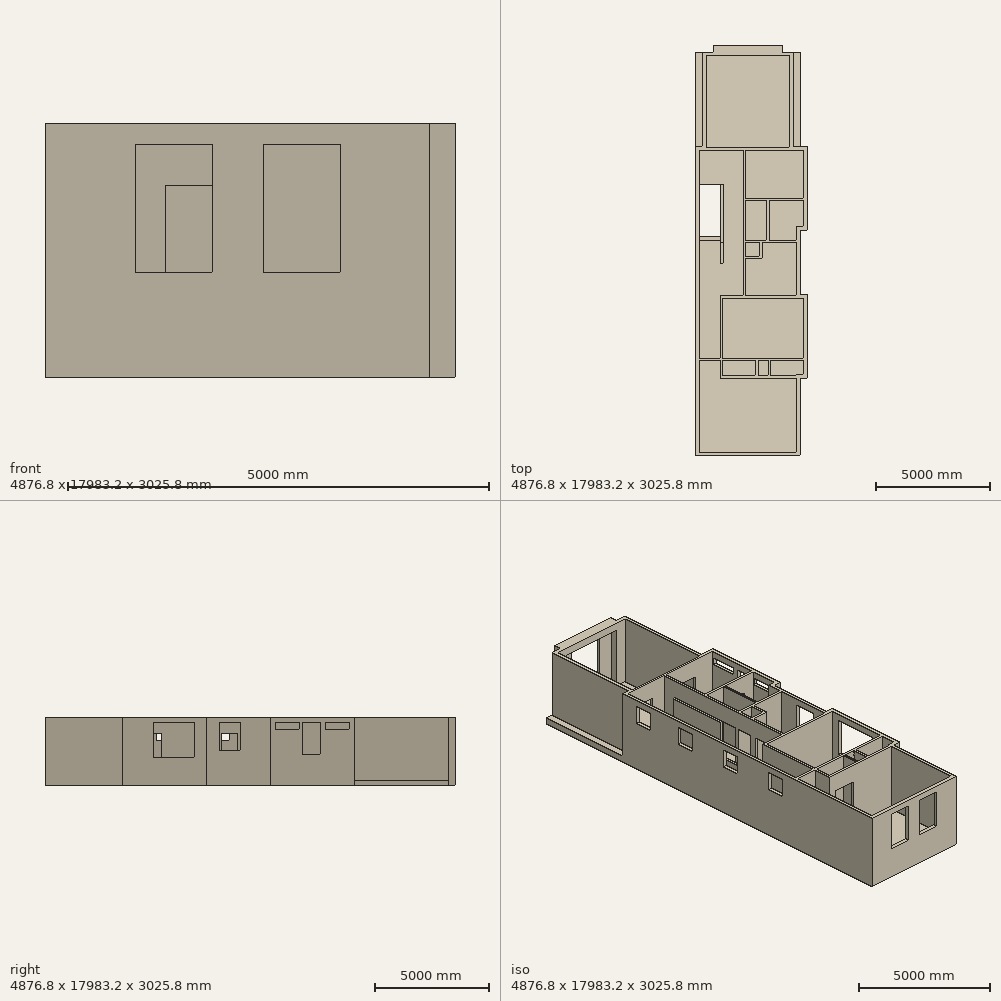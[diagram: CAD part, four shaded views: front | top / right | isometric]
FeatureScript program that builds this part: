
annotation { "Feature Type Name" : "Feature", "Feature Type Description" : "" }
export const myFeature = defineFeature(function(context is Context, id is Id, definition is map)
    precondition{}
    {
        {
            var Q0;
            Q0=qCreatedBy(makeId("Top.planeOp"),FACE);
            var sketch = newSketch(context, id + "F0", { "sketchPlane" : qUnion([Q0])});
            skLineSegment(sketch, "E0", {"start": v(4572, 0) * mm, "end": v(0, 0) * mm});
            skLineSegment(sketch, "E1", {"start": v(0, 0) * mm, "end": v(0, 17678.4) * mm});
            skLineSegment(sketch, "E2", {"start": v(0, 17678.4) * mm, "end": v(762, 17678.4) * mm});
            skLineSegment(sketch, "E3", {"start": v(762, 17678.4) * mm, "end": v(762, 17983.2) * mm});
            skLineSegment(sketch, "E4", {"start": v(762, 17983.2) * mm, "end": v(3810, 17983.2) * mm});
            skLineSegment(sketch, "E5", {"start": v(3810, 17983.2) * mm, "end": v(3810, 17678.4) * mm});
            skLineSegment(sketch, "E6", {"start": v(3810, 17678.4) * mm, "end": v(4572, 17678.4) * mm});
            skLineSegment(sketch, "E7", {"start": v(4572, 17678.4) * mm, "end": v(4572, 13538.2) * mm});
            skLineSegment(sketch, "E8", {"start": v(4572, 13538.2) * mm, "end": v(4876.8, 13538.2) * mm});
            skLineSegment(sketch, "E9", {"start": v(4876.8, 13538.2) * mm, "end": v(4876.8, 9880.6) * mm});
            skLineSegment(sketch, "E10", {"start": v(4876.8, 9880.6) * mm, "end": v(4572, 9880.6) * mm});
            skLineSegment(sketch, "E11", {"start": v(4572, 9880.6) * mm, "end": v(4572, 7048.5) * mm});
            skLineSegment(sketch, "E12", {"start": v(4572, 7048.5) * mm, "end": v(4876.8, 7048.5) * mm});
            skLineSegment(sketch, "E13", {"start": v(4876.8, 7048.5) * mm, "end": v(4876.8, 3390.9) * mm});
            skLineSegment(sketch, "E14", {"start": v(4876.8, 3390.9) * mm, "end": v(4572, 3390.9) * mm});
            skLineSegment(sketch, "E15", {"start": v(4572, 3390.9) * mm, "end": v(4572, 0) * mm});
            skSolve(sketch);
        }
        {
            var Q0;
            Q0=makeQuery(id+"F0.imprint","IMPRINT",FACE,{"disambiguationData":[TD([[makeQuery(id+"F0.imprint","IMPRINT",EDGE,{"derivedFrom":sQuery(id+"F0.wireOp",EDGE,"E0")}),-1.0]])]});
            extrude(context, id + "F1", {"entities" : qUnion([Q0]), "oppositeDirection" : true, "depth" : 254 * mm});
        }
        {
            var Q0;
            Q0=makeQuery(id+"F1.opExtrude","CAP_FACE",FACE,{"disambiguationData":[OSD([sQuery(id+"F0.wireOp",EDGE,"E0"),sQuery(id+"F0.wireOp",EDGE,"E1"),sQuery(id+"F0.wireOp",EDGE,"E2"),sQuery(id+"F0.wireOp",EDGE,"E3"),sQuery(id+"F0.wireOp",EDGE,"E4"),sQuery(id+"F0.wireOp",EDGE,"E5"),sQuery(id+"F0.wireOp",EDGE,"E6"),sQuery(id+"F0.wireOp",EDGE,"E7"),sQuery(id+"F0.wireOp",EDGE,"E8"),sQuery(id+"F0.wireOp",EDGE,"E9"),sQuery(id+"F0.wireOp",EDGE,"E10"),sQuery(id+"F0.wireOp",EDGE,"E11"),sQuery(id+"F0.wireOp",EDGE,"E12"),sQuery(id+"F0.wireOp",EDGE,"E13"),sQuery(id+"F0.wireOp",EDGE,"E14"),sQuery(id+"F0.wireOp",EDGE,"E15")])],"isStart":true});
            var sketch = newSketch(context, id + "F2", { "sketchPlane" : qUnion([Q0])});
            skLineSegment(sketch, "E16", {"start": v(0, 17678.4) * mm, "end": v(304.8, 17678.4) * mm});
            skLineSegment(sketch, "E17", {"start": v(304.8, 17678.4) * mm, "end": v(4267.2, 17678.4) * mm, "construction": true});
            skLineSegment(sketch, "E18", {"start": v(4267.2, 17678.4) * mm, "end": v(4572, 17678.4) * mm});
            skLineSegment(sketch, "E19", {"start": v(304.8, 17678.4) * mm, "end": v(304.8, 13538.2) * mm});
            skLineSegment(sketch, "E20", {"start": v(4267.2, 17678.4) * mm, "end": v(4267.2, 13538.2) * mm});
            skLineSegment(sketch, "E21", {"start": v(4267.2, 13538.2) * mm, "end": v(4572, 13538.2) * mm});
            skLineSegment(sketch, "E22", {"start": v(4572, 13538.2) * mm, "end": v(4572, 17678.4) * mm});
            skLineSegment(sketch, "E23", {"start": v(304.8, 13538.2) * mm, "end": v(0, 13538.2) * mm});
            skLineSegment(sketch, "E24", {"start": v(0, 13538.2) * mm, "end": v(0, 17678.4) * mm});
            skSolve(sketch);
        }
        {
            var Q0;
            {var subQ2=sQuery(id+"F2.wireOp",EDGE,"E19");Q0=makeQuery(id+"F2.imprint","IMPRINT",FACE,{"disambiguationData":[TD([[makeQuery(id+"F2.imprint","IMPRINT",EDGE,{"derivedFrom":subQ2}),1.0]])]});}
            var sketch = newSketch(context, id + "F3", { "sketchPlane" : qUnion([Q0])});
            skLineSegment(sketch, "E25.0", {"start": v(4724.4, 13385.8) * mm, "end": v(4572, 13385.8) * mm});
            skLineSegment(sketch, "E25.1", {"start": v(4724.4, 10033) * mm, "end": v(4724.4, 13385.8) * mm});
            skLineSegment(sketch, "E25.2", {"start": v(4419.6, 10033) * mm, "end": v(4724.4, 10033) * mm});
            skLineSegment(sketch, "E25.3", {"start": v(4419.6, 6896.1) * mm, "end": v(4419.6, 10033) * mm});
            skLineSegment(sketch, "E25.4", {"start": v(4724.4, 6896.1) * mm, "end": v(4419.6, 6896.1) * mm});
            skLineSegment(sketch, "E25.5", {"start": v(4572, 13385.8) * mm, "end": v(4114.8, 13385.8) * mm});
            skLineSegment(sketch, "E25.6", {"start": v(4724.4, 3543.3) * mm, "end": v(4724.4, 6896.1) * mm});
            skLineSegment(sketch, "E25.7", {"start": v(4419.6, 3543.3) * mm, "end": v(4724.4, 3543.3) * mm});
            skLineSegment(sketch, "E25.8", {"start": v(4419.6, 152.4) * mm, "end": v(4419.6, 3543.3) * mm});
            skLineSegment(sketch, "E25.9", {"start": v(3657.6, 17830.8) * mm, "end": v(914.4, 17830.8) * mm});
            skLineSegment(sketch, "E25.10", {"start": v(3657.6, 17526) * mm, "end": v(3657.6, 17830.8) * mm});
            skLineSegment(sketch, "E25.11", {"start": v(4114.8, 17526) * mm, "end": v(3657.6, 17526) * mm});
            skLineSegment(sketch, "E25.12", {"start": v(4114.8, 13385.8) * mm, "end": v(4114.8, 17526) * mm});
            skLineSegment(sketch, "E25.13", {"start": v(914.4, 17830.8) * mm, "end": v(914.4, 17526) * mm});
            skLineSegment(sketch, "E25.14", {"start": v(914.4, 17526) * mm, "end": v(457.2, 17526) * mm});
            skLineSegment(sketch, "E25.15", {"start": v(457.2, 17526) * mm, "end": v(457.2, 13385.8) * mm});
            skLineSegment(sketch, "E25.16", {"start": v(457.2, 13385.8) * mm, "end": v(152.4, 13385.8) * mm});
            skLineSegment(sketch, "E25.17", {"start": v(152.4, 13385.8) * mm, "end": v(152.4, 152.4) * mm});
            skLineSegment(sketch, "E25.18", {"start": v(152.4, 152.4) * mm, "end": v(4419.6, 152.4) * mm});
            skSolve(sketch);
        }
        {
            var Q0;
            Q0=makeQuery(id+"F3.imprint","IMPRINT",FACE,{"disambiguationData":[TD([[makeQuery(id+"F3.imprint","IMPRINT",EDGE,{"derivedFrom":sQuery(id+"F3.wireOp",EDGE,"E25.0")}),-1.0]])]});
            extrude(context, id + "F4", {"entities" : qUnion([Q0]), "operationType" : NewBodyOperationType.ADD, "depth" : 2743.2 * mm + 28.57 * mm});
        }
        {
            var Q0;
            {var subQ2=sQuery(id+"F2.wireOp",EDGE,"E19");Q0=makeQuery(id+"F2.imprint","IMPRINT",FACE,{"disambiguationData":[TD([[makeQuery(id+"F2.imprint","IMPRINT",EDGE,{"derivedFrom":subQ2}),1.0]])]});}
            var sketch = newSketch(context, id + "F5", { "sketchPlane" : qUnion([Q0])});
            skLineSegment(sketch, "E26", {"start": v(457.2, 13385.8) * mm, "end": v(2095.5, 13385.8) * mm});
            skLineSegment(sketch, "E27", {"start": v(2095.5, 13385.8) * mm, "end": v(2095.5, 6997.7) * mm});
            skLineSegment(sketch, "E28", {"start": v(2095.5, 6997.7) * mm, "end": v(1066.8, 6997.7) * mm});
            skLineSegment(sketch, "E29", {"start": v(1066.8, 6997.7) * mm, "end": v(1066.8, 4267.2) * mm});
            skLineSegment(sketch, "E30", {"start": v(1066.8, 4267.2) * mm, "end": v(152.4, 4267.2) * mm});
            skLineSegment(sketch, "E31", {"start": v(1066.8, 4165.6) * mm, "end": v(152.4, 4165.6) * mm});
            skLineSegment(sketch, "E32", {"start": v(1066.8, 4165.6) * mm, "end": v(1066.8, 3390.9) * mm});
            skLineSegment(sketch, "E33", {"start": v(1066.8, 3390.9) * mm, "end": v(4419.6, 3390.9) * mm});
            skLineSegment(sketch, "E34", {"start": v(3276.6, 4165.6) * mm, "end": v(3276.6, 3492.5) * mm});
            skLineSegment(sketch, "E35", {"start": v(3276.6, 3492.5) * mm, "end": v(4419.6, 3492.5) * mm});
            skLineSegment(sketch, "E36", {"start": v(1168.4, 4267.2) * mm, "end": v(4724.4, 4267.2) * mm});
            skLineSegment(sketch, "E37", {"start": v(3276.6, 4165.6) * mm, "end": v(4724.4, 4165.6) * mm});
            skLineSegment(sketch, "E38.bottom", {"start": v(1168.4, 4165.6) * mm, "end": v(2628.9, 4165.6) * mm});
            skLineSegment(sketch, "E38.top", {"start": v(1168.4, 3492.5) * mm, "end": v(2628.9, 3492.5) * mm});
            skLineSegment(sketch, "E38.left", {"start": v(1168.4, 4165.6) * mm, "end": v(1168.4, 3492.5) * mm});
            skLineSegment(sketch, "E38.right", {"start": v(2628.9, 4165.6) * mm, "end": v(2628.9, 3492.5) * mm});
            skLineSegment(sketch, "E39.bottom", {"start": v(2730.5, 4165.6) * mm, "end": v(3175, 4165.6) * mm});
            skLineSegment(sketch, "E39.top", {"start": v(2730.5, 3492.5) * mm, "end": v(3175, 3492.5) * mm});
            skLineSegment(sketch, "E39.left", {"start": v(2730.5, 4165.6) * mm, "end": v(2730.5, 3492.5) * mm});
            skLineSegment(sketch, "E39.right", {"start": v(3175, 4165.6) * mm, "end": v(3175, 3492.5) * mm});
            skLineSegment(sketch, "E40", {"start": v(152.4, 4267.2) * mm, "end": v(152.4, 4165.6) * mm});
            skLineSegment(sketch, "E41", {"start": v(4724.4, 4267.2) * mm, "end": v(4724.4, 4165.6) * mm});
            skLineSegment(sketch, "E42", {"start": v(4419.6, 3492.5) * mm, "end": v(4419.6, 3390.9) * mm});
            skLineSegment(sketch, "E43", {"start": v(1168.4, 4267.2) * mm, "end": v(1168.4, 6896.1) * mm});
            skLineSegment(sketch, "E44", {"start": v(1168.4, 6896.1) * mm, "end": v(4419.6, 6896.1) * mm});
            skLineSegment(sketch, "E45", {"start": v(2197.1, 6997.7) * mm, "end": v(4419.6, 6997.7) * mm});
            skLineSegment(sketch, "E46", {"start": v(2197.1, 6997.7) * mm, "end": v(2197.1, 8623.3) * mm});
            skLineSegment(sketch, "E47", {"start": v(4419.6, 6997.7) * mm, "end": v(4419.6, 6896.1) * mm});
            skLineSegment(sketch, "E48", {"start": v(2197.1, 8623.3) * mm, "end": v(2908.3, 8623.3) * mm});
            skLineSegment(sketch, "E49", {"start": v(2908.3, 8623.3) * mm, "end": v(2908.3, 9334.5) * mm});
            skLineSegment(sketch, "E50", {"start": v(2908.3, 9334.5) * mm, "end": v(4419.6, 9334.5) * mm});
            skLineSegment(sketch, "E51.bottom", {"start": v(2197.1, 9334.5) * mm, "end": v(2806.7, 9334.5) * mm});
            skLineSegment(sketch, "E51.top", {"start": v(2197.1, 8724.9) * mm, "end": v(2806.7, 8724.9) * mm});
            skLineSegment(sketch, "E51.left", {"start": v(2197.1, 9334.5) * mm, "end": v(2197.1, 8724.9) * mm});
            skLineSegment(sketch, "E51.right", {"start": v(2806.7, 9334.5) * mm, "end": v(2806.7, 8724.9) * mm});
            skLineSegment(sketch, "E52.bottom", {"start": v(2197.1, 11176) * mm, "end": v(3111.5, 11176) * mm});
            skLineSegment(sketch, "E52.top", {"start": v(2197.1, 9436.1) * mm, "end": v(3111.5, 9436.1) * mm});
            skLineSegment(sketch, "E52.left", {"start": v(2197.1, 11176) * mm, "end": v(2197.1, 9436.1) * mm});
            skLineSegment(sketch, "E52.right", {"start": v(3111.5, 11176) * mm, "end": v(3111.5, 9436.1) * mm});
            skLineSegment(sketch, "E53", {"start": v(4419.6, 9436.1) * mm, "end": v(3213.1, 9436.1) * mm});
            skLineSegment(sketch, "E54", {"start": v(3213.1, 9436.1) * mm, "end": v(3213.1, 11176) * mm});
            skLineSegment(sketch, "E55", {"start": v(3213.1, 11176) * mm, "end": v(4724.4, 11176) * mm});
            skLineSegment(sketch, "E56", {"start": v(4419.6, 9436.1) * mm, "end": v(4419.6, 9334.5) * mm});
            skLineSegment(sketch, "E57", {"start": v(4724.4, 11277.6) * mm, "end": v(2197.1, 11277.6) * mm});
            skLineSegment(sketch, "E58", {"start": v(4724.4, 11277.6) * mm, "end": v(4724.4, 11176) * mm});
            skLineSegment(sketch, "E59", {"start": v(2197.1, 11277.6) * mm, "end": v(2197.1, 13385.8) * mm});
            skLineSegment(sketch, "E60", {"start": v(2197.1, 13385.8) * mm, "end": v(4114.8, 13385.8) * mm});
            skLineSegment(sketch, "E61", {"start": v(457.2, 13487.4) * mm, "end": v(4114.8, 13487.4) * mm});
            skLineSegment(sketch, "E62", {"start": v(4114.8, 13487.4) * mm, "end": v(4114.8, 13385.8) * mm});
            skLineSegment(sketch, "E63", {"start": v(457.2, 13487.4) * mm, "end": v(457.2, 13385.8) * mm});
            skSolve(sketch);
        }
        {
            var Q0;
            Q0=makeQuery(id+"F5.imprint","IMPRINT",FACE,{"disambiguationData":[TD([[makeQuery(id+"F5.imprint","IMPRINT",EDGE,{"derivedFrom":sQuery(id+"F5.wireOp",EDGE,"E26")}),1.0]])]});
            var Q1;
            Q1=sQuery(id+"F5.wireOp",EDGE,"E59");
            var Q2;
            Q2=sQuery(id+"F5.wireOp",EDGE,"E27");
            var Q3;
            Q3=sQuery(id+"F5.wireOp",EDGE,"E26");
            var Q4;
            Q4=sQuery(id+"F5.wireOp",EDGE,"E63");
            var Q5;
            Q5=sQuery(id+"F5.wireOp",EDGE,"E61");
            var Q6;
            Q6=sQuery(id+"F5.wireOp",EDGE,"E60");
            var Q7;
            Q7=sQuery(id+"F5.wireOp",EDGE,"E62");
            var Q8;
            Q8=sQuery(id+"F5.wireOp",EDGE,"E57");
            var Q9;
            Q9=sQuery(id+"F5.wireOp",EDGE,"E52.bottom");
            var Q10;
            Q10=sQuery(id+"F5.wireOp",EDGE,"E52.left");
            var Q11;
            Q11=sQuery(id+"F5.wireOp",EDGE,"E52.right");
            var Q12;
            Q12=sQuery(id+"F5.wireOp",EDGE,"E52.top");
            var Q13;
            Q13=sQuery(id+"F5.wireOp",EDGE,"E54");
            var Q14;
            Q14=sQuery(id+"F5.wireOp",EDGE,"E55");
            var Q15;
            Q15=sQuery(id+"F5.wireOp",EDGE,"E58");
            var Q16;
            Q16=sQuery(id+"F5.wireOp",EDGE,"E53");
            var Q17;
            Q17=sQuery(id+"F5.wireOp",EDGE,"E56");
            var Q18;
            Q18=sQuery(id+"F5.wireOp",EDGE,"E50");
            var Q19;
            Q19=sQuery(id+"F5.wireOp",EDGE,"E49");
            var Q20;
            Q20=sQuery(id+"F5.wireOp",EDGE,"E48");
            var Q21;
            Q21=sQuery(id+"F5.wireOp",EDGE,"E51.right");
            var Q22;
            Q22=sQuery(id+"F5.wireOp",EDGE,"E51.bottom");
            var Q23;
            Q23=sQuery(id+"F5.wireOp",EDGE,"E51.left");
            var Q24;
            Q24=sQuery(id+"F5.wireOp",EDGE,"E51.top");
            var Q25;
            Q25=sQuery(id+"F5.wireOp",EDGE,"E46");
            var Q26;
            Q26=sQuery(id+"F5.wireOp",EDGE,"E45");
            var Q27;
            Q27=sQuery(id+"F5.wireOp",EDGE,"E47");
            var Q28;
            Q28=sQuery(id+"F5.wireOp",EDGE,"E44");
            var Q29;
            Q29=sQuery(id+"F5.wireOp",EDGE,"E28");
            var Q30;
            Q30=sQuery(id+"F5.wireOp",EDGE,"E29");
            var Q31;
            Q31=sQuery(id+"F5.wireOp",EDGE,"E43");
            var Q32;
            Q32=sQuery(id+"F5.wireOp",EDGE,"E30");
            var Q33;
            Q33=sQuery(id+"F5.wireOp",EDGE,"E40");
            var Q34;
            Q34=sQuery(id+"F5.wireOp",EDGE,"E31");
            var Q35;
            Q35=sQuery(id+"F5.wireOp",EDGE,"E32");
            var Q36;
            Q36=sQuery(id+"F5.wireOp",EDGE,"E36");
            var Q37;
            Q37=sQuery(id+"F5.wireOp",EDGE,"E38.bottom");
            var Q38;
            Q38=sQuery(id+"F5.wireOp",EDGE,"E38.left");
            var Q39;
            Q39=sQuery(id+"F5.wireOp",EDGE,"E38.top");
            var Q40;
            Q40=sQuery(id+"F5.wireOp",EDGE,"E38.right");
            var Q41;
            Q41=sQuery(id+"F5.wireOp",EDGE,"E33");
            var Q42;
            Q42=sQuery(id+"F5.wireOp",EDGE,"E35");
            var Q43;
            Q43=sQuery(id+"F5.wireOp",EDGE,"E42");
            var Q44;
            Q44=sQuery(id+"F5.wireOp",EDGE,"E41");
            var Q45;
            Q45=sQuery(id+"F5.wireOp",EDGE,"E37");
            var Q46;
            Q46=sQuery(id+"F5.wireOp",EDGE,"E34");
            var Q47;
            Q47=sQuery(id+"F5.wireOp",EDGE,"E39.right");
            var Q48;
            Q48=sQuery(id+"F5.wireOp",EDGE,"E39.bottom");
            var Q49;
            Q49=sQuery(id+"F5.wireOp",EDGE,"E39.left");
            var Q50;
            Q50=sQuery(id+"F5.wireOp",EDGE,"E39.top");
            var Q51;
            Q51=makeQuery(id+"F4.opExtrude","CAP_FACE",FACE,{"disambiguationData":[OSD([sQuery(id+"F0.wireOp",EDGE,"E0"),sQuery(id+"F0.wireOp",EDGE,"E1"),sQuery(id+"F0.wireOp",EDGE,"E2"),sQuery(id+"F0.wireOp",EDGE,"E3"),sQuery(id+"F0.wireOp",EDGE,"E4"),sQuery(id+"F0.wireOp",EDGE,"E5"),sQuery(id+"F0.wireOp",EDGE,"E6"),sQuery(id+"F0.wireOp",EDGE,"E8"),sQuery(id+"F0.wireOp",EDGE,"E9"),sQuery(id+"F0.wireOp",EDGE,"E10"),sQuery(id+"F0.wireOp",EDGE,"E11"),sQuery(id+"F0.wireOp",EDGE,"E12"),sQuery(id+"F0.wireOp",EDGE,"E13"),sQuery(id+"F0.wireOp",EDGE,"E14"),sQuery(id+"F0.wireOp",EDGE,"E15"),sQuery(id+"F2.wireOp",EDGE,"E19"),sQuery(id+"F2.wireOp",EDGE,"E20"),sQuery(id+"F2.wireOp",EDGE,"E21"),sQuery(id+"F2.wireOp",EDGE,"E23"),sQuery(id+"F3.wireOp",EDGE,"E25.0"),sQuery(id+"F3.wireOp",EDGE,"E25.1"),sQuery(id+"F3.wireOp",EDGE,"E25.2"),sQuery(id+"F3.wireOp",EDGE,"E25.3"),sQuery(id+"F3.wireOp",EDGE,"E25.4"),sQuery(id+"F3.wireOp",EDGE,"E25.5"),sQuery(id+"F3.wireOp",EDGE,"E25.6"),sQuery(id+"F3.wireOp",EDGE,"E25.7"),sQuery(id+"F3.wireOp",EDGE,"E25.8"),sQuery(id+"F3.wireOp",EDGE,"E25.9"),sQuery(id+"F3.wireOp",EDGE,"E25.10"),sQuery(id+"F3.wireOp",EDGE,"E25.11"),sQuery(id+"F3.wireOp",EDGE,"E25.12"),sQuery(id+"F3.wireOp",EDGE,"E25.13"),sQuery(id+"F3.wireOp",EDGE,"E25.14"),sQuery(id+"F3.wireOp",EDGE,"E25.15"),sQuery(id+"F3.wireOp",EDGE,"E25.16"),sQuery(id+"F3.wireOp",EDGE,"E25.17"),sQuery(id+"F3.wireOp",EDGE,"E25.18")])],"isStart":false});
            extrude(context, id + "F6", {"entities" : qUnion([Q0]), "operationType" : NewBodyOperationType.ADD, "surfaceEntities" : qUnion([Q1, Q2, Q3, Q4, Q5, Q6, Q7, Q8, Q9, Q10, Q11, Q12, Q13, Q14, Q15, Q16, Q17, Q18, Q19, Q20, Q21, Q22, Q23, Q24, Q25, Q26, Q27, Q28, Q29, Q30, Q31, Q32, Q33, Q34, Q35, Q36, Q37, Q38, Q39, Q40, Q41, Q42, Q43, Q44, Q45, Q46, Q47, Q48, Q49, Q50]), "endBound" : BoundingType.UP_TO_SURFACE, "endBoundEntityFace" : qUnion([Q51]), "depth" : 30.48 * mm});
        }
        {
            var Q0;
            Q0=makeQuery(id+"F6.opExtrude","SWEPT_FACE",FACE,{"disambiguationData":[OSD([sQuery(id+"F5.wireOp",EDGE,"E61")])]});
            var sketch = newSketch(context, id + "F7", { "sketchPlane" : qUnion([Q0])});
            skLineSegment(sketch, "E64.bottom", {"start": v(-3810, 2032) * mm, "end": v(-3098.8, 2032) * mm});
            skLineSegment(sketch, "E64.top", {"start": v(-3810, 0) * mm, "end": v(-3098.8, 0) * mm});
            skLineSegment(sketch, "E64.left", {"start": v(-3810, 2032) * mm, "end": v(-3810, 0) * mm});
            skLineSegment(sketch, "E64.right", {"start": v(-3098.8, 2032) * mm, "end": v(-3098.8, 0) * mm});
            skLineSegment(sketch, "E65.bottom", {"start": v(-1473.2, 2032) * mm, "end": v(-711.2, 2032) * mm});
            skLineSegment(sketch, "E65.top", {"start": v(-1473.2, 0) * mm, "end": v(-711.2, 0) * mm});
            skLineSegment(sketch, "E65.left", {"start": v(-1473.2, 2032) * mm, "end": v(-1473.2, 0) * mm});
            skLineSegment(sketch, "E65.right", {"start": v(-711.2, 2032) * mm, "end": v(-711.2, 0) * mm});
            skSolve(sketch);
        }
        {
            var Q0;
            Q0=makeQuery(id+"F7.imprint","IMPRINT",FACE,{"disambiguationData":[TD([[makeQuery(id+"F7.imprint","IMPRINT",EDGE,{"derivedFrom":sQuery(id+"F7.wireOp",EDGE,"E64.bottom")}),-1.0]])]});
            var Q1;
            Q1=makeQuery(id+"F7.imprint","IMPRINT",FACE,{"disambiguationData":[TD([[makeQuery(id+"F7.imprint","IMPRINT",EDGE,{"derivedFrom":sQuery(id+"F7.wireOp",EDGE,"E65.bottom")}),-1.0]])]});
            extrude(context, id + "F8", {"entities" : qUnion([Q0, Q1]), "operationType" : NewBodyOperationType.REMOVE, "endBound" : BoundingType.UP_TO_NEXT, "oppositeDirection" : true, "depth" : 30.48 * mm});
        }
        {
            var Q0;
            Q0=makeQuery(id+"F6.opExtrude","SWEPT_FACE",FACE,{"disambiguationData":[OSD([sQuery(id+"F5.wireOp",EDGE,"E55")])]});
            var sketch = newSketch(context, id + "F9", { "sketchPlane" : qUnion([Q0])});
            skLineSegment(sketch, "E66.bottom", {"start": v(3517.9, 2032) * mm, "end": v(4229.1, 2032) * mm});
            skLineSegment(sketch, "E66.top", {"start": v(3517.9, 0) * mm, "end": v(4229.1, 0) * mm});
            skLineSegment(sketch, "E66.left", {"start": v(3517.9, 2032) * mm, "end": v(3517.9, 0) * mm});
            skLineSegment(sketch, "E66.right", {"start": v(4229.1, 2032) * mm, "end": v(4229.1, 0) * mm});
            skSolve(sketch);
        }
        {
            var Q0;
            Q0=makeQuery(id+"F9.imprint","IMPRINT",FACE,{"disambiguationData":[TD([[makeQuery(id+"F9.imprint","IMPRINT",EDGE,{"derivedFrom":sQuery(id+"F9.wireOp",EDGE,"E66.bottom")}),-1.0]])]});
            extrude(context, id + "F10", {"entities" : qUnion([Q0]), "operationType" : NewBodyOperationType.REMOVE, "endBound" : BoundingType.UP_TO_NEXT, "oppositeDirection" : true, "depth" : 30.48 * mm});
        }
        {
            var Q0;
            Q0=makeQuery(id+"F6.opExtrude","SWEPT_FACE",FACE,{"disambiguationData":[OSD([sQuery(id+"F5.wireOp",EDGE,"E27")])]});
            var sketch = newSketch(context, id + "F11", { "sketchPlane" : qUnion([Q0])});
            skLineSegment(sketch, "E67.top", {"start": v(-11068.05, 0) * mm, "end": v(-9544.05, 0) * mm});
            skLineSegment(sketch, "E67.left", {"start": v(-11068.05, 2032) * mm, "end": v(-11068.05, 0) * mm});
            skLineSegment(sketch, "E67.right", {"start": v(-9544.05, 2032) * mm, "end": v(-9544.05, 0) * mm});
            skLineSegment(sketch, "E68.top", {"start": v(-9334.5, 0) * mm, "end": v(-8724.9, 0) * mm});
            skLineSegment(sketch, "E68.left", {"start": v(-9334.5, 2032) * mm, "end": v(-9334.5, 0) * mm});
            skLineSegment(sketch, "E68.right", {"start": v(-8724.9, 2032) * mm, "end": v(-8724.9, 0) * mm});
            skLineSegment(sketch, "E69.bottom", {"start": v(-8420.1, 2032) * mm, "end": v(-7708.9, 2032) * mm});
            skLineSegment(sketch, "E69.top", {"start": v(-8420.1, 0) * mm, "end": v(-7708.9, 0) * mm});
            skLineSegment(sketch, "E69.left", {"start": v(-8420.1, 2032) * mm, "end": v(-8420.1, 0) * mm});
            skLineSegment(sketch, "E69.right", {"start": v(-7708.9, 2032) * mm, "end": v(-7708.9, 0) * mm});
            skLineSegment(sketch, "E70", {"start": v(-9334.5, 2032) * mm, "end": v(-9029.7, 2032) * mm});
            skLineSegment(sketch, "E71", {"start": v(-9029.7, 2032) * mm, "end": v(-8724.9, 2032) * mm});
            skLineSegment(sketch, "E72", {"start": v(-9334.5, 2771.78) * mm, "end": v(-9029.7, 2771.78) * mm, "construction": true});
            skLineSegment(sketch, "E73", {"start": v(-9029.7, 2771.78) * mm, "end": v(-8724.9, 2771.78) * mm, "construction": true});
            skLineSegment(sketch, "E74", {"start": v(-11176, 2771.78) * mm, "end": v(-10306.05, 2771.78) * mm, "construction": true});
            skLineSegment(sketch, "E75", {"start": v(-10306.05, 2771.78) * mm, "end": v(-9436.1, 2771.78) * mm, "construction": true});
            skLineSegment(sketch, "E76", {"start": v(-11068.05, 2032) * mm, "end": v(-10306.05, 2032) * mm});
            skLineSegment(sketch, "E77", {"start": v(-10306.05, 2032) * mm, "end": v(-9544.05, 2032) * mm});
            skSolve(sketch);
        }
        {
            var Q0;
            Q0=makeQuery(id+"F11.imprint","IMPRINT",FACE,{"disambiguationData":[TD([[makeQuery(id+"F11.imprint","IMPRINT",EDGE,{"derivedFrom":sQuery(id+"F11.wireOp",EDGE,"E69.bottom")}),-1.0]])]});
            var Q1;
            Q1=makeQuery(id+"F11.imprint","IMPRINT",FACE,{"disambiguationData":[TD([[makeQuery(id+"F11.imprint","IMPRINT",EDGE,{"derivedFrom":sQuery(id+"F11.wireOp",EDGE,"E68.top")}),1.0]])]});
            var Q2;
            Q2=makeQuery(id+"F11.imprint","IMPRINT",FACE,{"disambiguationData":[TD([[makeQuery(id+"F11.imprint","IMPRINT",EDGE,{"derivedFrom":sQuery(id+"F11.wireOp",EDGE,"E67.top")}),1.0]])]});
            extrude(context, id + "F12", {"entities" : qUnion([Q0, Q1, Q2]), "operationType" : NewBodyOperationType.REMOVE, "endBound" : BoundingType.UP_TO_NEXT, "oppositeDirection" : true, "depth" : 30.48 * mm});
        }
        {
            var Q0;
            Q0=makeQuery(id+"F6.opExtrude","SWEPT_FACE",FACE,{"disambiguationData":[OSD([sQuery(id+"F5.wireOp",EDGE,"E30")])]});
            var sketch = newSketch(context, id + "F13", { "sketchPlane" : qUnion([Q0])});
            skLineSegment(sketch, "E78.bottom", {"start": v(-990.6, 2032) * mm, "end": v(-228.6, 2032) * mm});
            skLineSegment(sketch, "E78.top", {"start": v(-990.6, 0) * mm, "end": v(-228.6, 0) * mm});
            skLineSegment(sketch, "E78.left", {"start": v(-990.6, 2032) * mm, "end": v(-990.6, 0) * mm});
            skLineSegment(sketch, "E78.right", {"start": v(-228.6, 2032) * mm, "end": v(-228.6, 0) * mm});
            skLineSegment(sketch, "E79", {"start": v(-1066.8, 0) * mm, "end": v(-990.6, 0) * mm, "construction": true});
            skLineSegment(sketch, "E80", {"start": v(-152.4, 0) * mm, "end": v(-228.6, 0) * mm, "construction": true});
            skSolve(sketch);
        }
        {
            var Q0;
            Q0=makeQuery(id+"F13.imprint","IMPRINT",FACE,{"disambiguationData":[TD([[makeQuery(id+"F13.imprint","IMPRINT",EDGE,{"derivedFrom":sQuery(id+"F13.wireOp",EDGE,"E78.bottom")}),-1.0]])]});
            extrude(context, id + "F14", {"entities" : qUnion([Q0]), "operationType" : NewBodyOperationType.REMOVE, "endBound" : BoundingType.UP_TO_NEXT, "oppositeDirection" : true, "depth" : 30.48 * mm});
        }
        {
            var Q0;
            Q0=makeQuery(id+"F6.opExtrude","SWEPT_FACE",FACE,{"disambiguationData":[OSD([sQuery(id+"F5.wireOp",EDGE,"E29")])]});
            var sketch = newSketch(context, id + "F15", { "sketchPlane" : qUnion([Q0])});
            skLineSegment(sketch, "E81.bottom", {"start": v(-5105.4, 2032) * mm, "end": v(-4343.4, 2032) * mm});
            skLineSegment(sketch, "E81.top", {"start": v(-5105.4, 0) * mm, "end": v(-4343.4, 0) * mm});
            skLineSegment(sketch, "E81.left", {"start": v(-5105.4, 2032) * mm, "end": v(-5105.4, 0) * mm});
            skLineSegment(sketch, "E81.right", {"start": v(-4343.4, 2032) * mm, "end": v(-4343.4, 0) * mm});
            skLineSegment(sketch, "E82", {"start": v(-4267.2, 0) * mm, "end": v(-4343.4, 0) * mm, "construction": true});
            skSolve(sketch);
        }
        {
            var Q0;
            Q0=makeQuery(id+"F15.imprint","IMPRINT",FACE,{"disambiguationData":[TD([[makeQuery(id+"F15.imprint","IMPRINT",EDGE,{"derivedFrom":sQuery(id+"F15.wireOp",EDGE,"E81.bottom")}),-1.0]])]});
            extrude(context, id + "F16", {"entities" : qUnion([Q0]), "operationType" : NewBodyOperationType.REMOVE, "endBound" : BoundingType.UP_TO_NEXT, "oppositeDirection" : true, "depth" : 30.48 * mm});
        }
        {
            var Q0;
            Q0=makeQuery(id+"F6.opExtrude","SWEPT_FACE",FACE,{"disambiguationData":[OSD([sQuery(id+"F5.wireOp",EDGE,"E36")])]});
            var sketch = newSketch(context, id + "F17", { "sketchPlane" : qUnion([Q0])});
            skLineSegment(sketch, "E83.bottom", {"start": v(-4470.4, 2032) * mm, "end": v(-3530.6, 2032) * mm});
            skLineSegment(sketch, "E83.top", {"start": v(-4470.4, 0) * mm, "end": v(-3530.6, 0) * mm});
            skLineSegment(sketch, "E83.left", {"start": v(-4470.4, 2032) * mm, "end": v(-4470.4, 0) * mm});
            skLineSegment(sketch, "E83.right", {"start": v(-3530.6, 2032) * mm, "end": v(-3530.6, 0) * mm});
            skSolve(sketch);
        }
        {
            var Q0;
            Q0=makeQuery(id+"F17.imprint","IMPRINT",FACE,{"disambiguationData":[TD([[makeQuery(id+"F17.imprint","IMPRINT",EDGE,{"derivedFrom":sQuery(id+"F17.wireOp",EDGE,"E83.bottom")}),-1.0]])]});
            extrude(context, id + "F18", {"entities" : qUnion([Q0]), "operationType" : NewBodyOperationType.REMOVE, "endBound" : BoundingType.UP_TO_NEXT, "oppositeDirection" : true, "depth" : 30.48 * mm});
        }
        {
            var Q0;
            Q0=makeQuery(id+"F6.opExtrude","SWEPT_FACE",FACE,{"disambiguationData":[OSD([sQuery(id+"F5.wireOp",EDGE,"E33")])]});
            var sketch = newSketch(context, id + "F19", { "sketchPlane" : qUnion([Q0])});
            skLineSegment(sketch, "E84.bottom", {"start": v(1422.4, 2032) * mm, "end": v(2374.9, 2032) * mm});
            skLineSegment(sketch, "E84.top", {"start": v(1422.4, 0) * mm, "end": v(2374.9, 0) * mm});
            skLineSegment(sketch, "E84.left", {"start": v(1422.4, 2032) * mm, "end": v(1422.4, 0) * mm});
            skLineSegment(sketch, "E84.right", {"start": v(2374.9, 2032) * mm, "end": v(2374.9, 0) * mm});
            skSolve(sketch);
        }
        {
            var Q0;
            Q0=makeQuery(id+"F19.imprint","IMPRINT",FACE,{"disambiguationData":[TD([[makeQuery(id+"F19.imprint","IMPRINT",EDGE,{"derivedFrom":sQuery(id+"F19.wireOp",EDGE,"E84.bottom")}),-1.0]])]});
            extrude(context, id + "F20", {"entities" : qUnion([Q0]), "operationType" : NewBodyOperationType.REMOVE, "endBound" : BoundingType.UP_TO_NEXT, "oppositeDirection" : true, "depth" : 30.48 * mm});
        }
        {
            var Q0;
            {var subQ0=sQuery(id+"F0.wireOp",EDGE,"E0");Q0=makeQuery(id+"F4.boolean.opBoolean","MERGE",FACE,{"derivedFrom":[makeQuery(id+"F1.opExtrude","SWEPT_FACE",FACE,{"disambiguationData":[OSD([subQ0])]}),makeQuery(id+"F4.opExtrude","SWEPT_FACE",FACE,{"disambiguationData":[OSD([subQ0])]})]});}
            var sketch = newSketch(context, id + "F21", { "sketchPlane" : qUnion([Q0])});
            skLineSegment(sketch, "E85.bottom", {"start": v(1066.8, 2517.78) * mm, "end": v(1981.2, 2517.78) * mm});
            skLineSegment(sketch, "E85.left", {"start": v(1066.8, 2517.78) * mm, "end": v(1066.8, 993.78) * mm});
            skLineSegment(sketch, "E85.right", {"start": v(1981.2, 2517.78) * mm, "end": v(1981.2, 993.78) * mm});
            skLineSegment(sketch, "E86.bottom", {"start": v(2590.8, 2517.78) * mm, "end": v(3505.2, 2517.78) * mm});
            skLineSegment(sketch, "E86.left", {"start": v(2590.8, 2517.78) * mm, "end": v(2590.8, 993.78) * mm});
            skLineSegment(sketch, "E86.right", {"start": v(3505.2, 2517.78) * mm, "end": v(3505.2, 993.78) * mm});
            skLineSegment(sketch, "E87", {"start": v(1066.8, 993.78) * mm, "end": v(1524, 993.77) * mm});
            skLineSegment(sketch, "E88", {"start": v(1524, 993.78) * mm, "end": v(1981.2, 993.78) * mm});
            skLineSegment(sketch, "E89", {"start": v(2590.8, 993.78) * mm, "end": v(3048, 993.78) * mm});
            skLineSegment(sketch, "E90", {"start": v(3048, 993.78) * mm, "end": v(3505.2, 993.78) * mm});
            skLineSegment(sketch, "E91", {"start": v(0, -254) * mm, "end": v(2286, -254) * mm, "construction": true});
            skLineSegment(sketch, "E92", {"start": v(2286, -254) * mm, "end": v(4572, -254) * mm, "construction": true});
            skLineSegment(sketch, "E93", {"start": v(2286, -254) * mm, "end": v(2286, 0) * mm, "construction": true});
            skSolve(sketch);
        }
        {
            var Q0;
            Q0=makeQuery(id+"F21.imprint","IMPRINT",FACE,{"disambiguationData":[TD([[makeQuery(id+"F21.imprint","IMPRINT",EDGE,{"derivedFrom":sQuery(id+"F21.wireOp",EDGE,"E85.bottom")}),-1.0]])]});
            var Q1;
            Q1=makeQuery(id+"F21.imprint","IMPRINT",FACE,{"disambiguationData":[TD([[makeQuery(id+"F21.imprint","IMPRINT",EDGE,{"derivedFrom":sQuery(id+"F21.wireOp",EDGE,"E86.bottom")}),-1.0]])]});
            extrude(context, id + "F22", {"entities" : qUnion([Q0, Q1]), "operationType" : NewBodyOperationType.REMOVE, "endBound" : BoundingType.UP_TO_NEXT, "oppositeDirection" : true, "depth" : 30.48 * mm});
        }
        {
            var Q0;
            {var subQ0=sQuery(id+"F0.wireOp",EDGE,"E13");Q0=makeQuery(id+"F4.boolean.opBoolean","MERGE",FACE,{"derivedFrom":[makeQuery(id+"F1.opExtrude","SWEPT_FACE",FACE,{"disambiguationData":[OSD([subQ0])]}),makeQuery(id+"F4.opExtrude","SWEPT_FACE",FACE,{"disambiguationData":[OSD([subQ0])]})]});}
            var sketch = newSketch(context, id + "F23", { "sketchPlane" : qUnion([Q0])});
            skLineSegment(sketch, "E94.bottom", {"start": v(4724.4, 2517.78) * mm, "end": v(6553.2, 2517.78) * mm});
            skLineSegment(sketch, "E94.left", {"start": v(4724.4, 2517.78) * mm, "end": v(4724.4, 993.78) * mm});
            skLineSegment(sketch, "E94.right", {"start": v(6553.2, 2517.78) * mm, "end": v(6553.2, 993.78) * mm});
            skLineSegment(sketch, "E95", {"start": v(4724.4, 993.78) * mm, "end": v(5638.8, 993.78) * mm});
            skLineSegment(sketch, "E96", {"start": v(5638.8, 993.78) * mm, "end": v(6553.2, 993.78) * mm});
            skSolve(sketch);
        }
        {
            var Q0;
            Q0=makeQuery(id+"F23.imprint","IMPRINT",FACE,{"disambiguationData":[TD([[makeQuery(id+"F23.imprint","IMPRINT",EDGE,{"derivedFrom":sQuery(id+"F23.wireOp",EDGE,"E94.bottom")}),-1.0]])]});
            extrude(context, id + "F24", {"entities" : qUnion([Q0]), "operationType" : NewBodyOperationType.REMOVE, "endBound" : BoundingType.UP_TO_NEXT, "oppositeDirection" : true, "depth" : 30.48 * mm});
        }
        {
            var Q0;
            {var subQ0=sQuery(id+"F0.wireOp",EDGE,"E11");Q0=makeQuery(id+"F4.boolean.opBoolean","MERGE",FACE,{"derivedFrom":[makeQuery(id+"F1.opExtrude","SWEPT_FACE",FACE,{"disambiguationData":[OSD([subQ0])]}),makeQuery(id+"F4.opExtrude","SWEPT_FACE",FACE,{"disambiguationData":[OSD([subQ0])]})]});}
            var sketch = newSketch(context, id + "F25", { "sketchPlane" : qUnion([Q0])});
            skLineSegment(sketch, "E97.bottom", {"start": v(7620, 2517.78) * mm, "end": v(8534.4, 2517.78) * mm});
            skLineSegment(sketch, "E97.left", {"start": v(7620, 2517.78) * mm, "end": v(7620, 1298.58) * mm});
            skLineSegment(sketch, "E97.right", {"start": v(8534.4, 2517.78) * mm, "end": v(8534.4, 1298.58) * mm});
            skLineSegment(sketch, "E98", {"start": v(7620, 1298.58) * mm, "end": v(8077.2, 1298.58) * mm});
            skLineSegment(sketch, "E99", {"start": v(8077.2, 1298.58) * mm, "end": v(8534.4, 1298.58) * mm});
            skSolve(sketch);
        }
        {
            var Q0;
            Q0=makeQuery(id+"F25.imprint","IMPRINT",FACE,{"disambiguationData":[TD([[makeQuery(id+"F25.imprint","IMPRINT",EDGE,{"derivedFrom":sQuery(id+"F25.wireOp",EDGE,"E97.bottom")}),-1.0]])]});
            extrude(context, id + "F26", {"entities" : qUnion([Q0]), "operationType" : NewBodyOperationType.REMOVE, "endBound" : BoundingType.UP_TO_NEXT, "oppositeDirection" : true, "depth" : 30.48 * mm});
        }
        {
            var Q0;
            {var subQ0=sQuery(id+"F0.wireOp",EDGE,"E9");Q0=makeQuery(id+"F4.boolean.opBoolean","MERGE",FACE,{"derivedFrom":[makeQuery(id+"F1.opExtrude","SWEPT_FACE",FACE,{"disambiguationData":[OSD([subQ0])]}),makeQuery(id+"F4.opExtrude","SWEPT_FACE",FACE,{"disambiguationData":[OSD([subQ0])]})]});}
            var sketch = newSketch(context, id + "F27", { "sketchPlane" : qUnion([Q0])});
            skLineSegment(sketch, "E100.bottom", {"start": v(10071.1, 2517.78) * mm, "end": v(11137.9, 2517.78) * mm});
            skLineSegment(sketch, "E100.left", {"start": v(10071.1, 2517.78) * mm, "end": v(10071.1, 2212.98) * mm});
            skLineSegment(sketch, "E100.right", {"start": v(11137.9, 2517.78) * mm, "end": v(11137.9, 2212.98) * mm});
            skLineSegment(sketch, "E101.bottom", {"start": v(11290.3, 2517.78) * mm, "end": v(12052.3, 2517.78) * mm});
            skLineSegment(sketch, "E101.left", {"start": v(11290.3, 2517.78) * mm, "end": v(11290.3, 1146.18) * mm});
            skLineSegment(sketch, "E101.right", {"start": v(12052.3, 2517.78) * mm, "end": v(12052.3, 1146.18) * mm});
            skLineSegment(sketch, "E102.bottom", {"start": v(12280.9, 2517.78) * mm, "end": v(13347.7, 2517.78) * mm});
            skLineSegment(sketch, "E102.left", {"start": v(12280.9, 2517.78) * mm, "end": v(12280.9, 2212.98) * mm});
            skLineSegment(sketch, "E102.right", {"start": v(13347.7, 2517.78) * mm, "end": v(13347.7, 2212.98) * mm});
            skLineSegment(sketch, "E103", {"start": v(10071.1, 2212.98) * mm, "end": v(10604.5, 2212.98) * mm});
            skLineSegment(sketch, "E104", {"start": v(10604.5, 2212.98) * mm, "end": v(11137.9, 2212.98) * mm});
            skLineSegment(sketch, "E105", {"start": v(11290.3, 1146.18) * mm, "end": v(11671.3, 1146.18) * mm});
            skLineSegment(sketch, "E106", {"start": v(11671.3, 1146.18) * mm, "end": v(12052.3, 1146.18) * mm});
            skLineSegment(sketch, "E107", {"start": v(12280.9, 2212.98) * mm, "end": v(12814.3, 2212.98) * mm});
            skLineSegment(sketch, "E108", {"start": v(12814.3, 2212.98) * mm, "end": v(13347.7, 2212.98) * mm});
            skSolve(sketch);
        }
        {
            var Q0;
            Q0=makeQuery(id+"F27.imprint","IMPRINT",FACE,{"disambiguationData":[TD([[makeQuery(id+"F27.imprint","IMPRINT",EDGE,{"derivedFrom":sQuery(id+"F27.wireOp",EDGE,"E100.bottom")}),-1.0]])]});
            var Q1;
            Q1=makeQuery(id+"F27.imprint","IMPRINT",FACE,{"disambiguationData":[TD([[makeQuery(id+"F27.imprint","IMPRINT",EDGE,{"derivedFrom":sQuery(id+"F27.wireOp",EDGE,"E101.bottom")}),-1.0]])]});
            var Q2;
            Q2=makeQuery(id+"F27.imprint","IMPRINT",FACE,{"disambiguationData":[TD([[makeQuery(id+"F27.imprint","IMPRINT",EDGE,{"derivedFrom":sQuery(id+"F27.wireOp",EDGE,"E102.bottom")}),-1.0]])]});
            extrude(context, id + "F28", {"entities" : qUnion([Q0, Q1, Q2]), "operationType" : NewBodyOperationType.REMOVE, "endBound" : BoundingType.UP_TO_NEXT, "oppositeDirection" : true, "depth" : 30.48 * mm});
        }
        {
            var Q0;
            {var subQ0=sQuery(id+"F0.wireOp",EDGE,"E4");Q0=makeQuery(id+"F4.boolean.opBoolean","MERGE",FACE,{"derivedFrom":[makeQuery(id+"F1.opExtrude","SWEPT_FACE",FACE,{"disambiguationData":[OSD([subQ0])]}),makeQuery(id+"F4.opExtrude","SWEPT_FACE",FACE,{"disambiguationData":[OSD([subQ0])]})]});}
            var sketch = newSketch(context, id + "F29", { "sketchPlane" : qUnion([Q0])});
            skLineSegment(sketch, "E109.bottom", {"start": v(-3048, 2212.98) * mm, "end": v(-1524, 2212.98) * mm});
            skLineSegment(sketch, "E109.top", {"start": v(-3048, 688.98) * mm, "end": v(-1524, 688.98) * mm});
            skLineSegment(sketch, "E109.left", {"start": v(-3048, 2212.98) * mm, "end": v(-3048, 688.98) * mm});
            skLineSegment(sketch, "E109.right", {"start": v(-1524, 2212.98) * mm, "end": v(-1524, 688.98) * mm});
            skLineSegment(sketch, "E110", {"start": v(-1524, 688.98) * mm, "end": v(-762, 688.98) * mm, "construction": true});
            skLineSegment(sketch, "E111", {"start": v(-3048, 688.98) * mm, "end": v(-3810, 688.98) * mm, "construction": true});
            skSolve(sketch);
        }
        {
            var Q0;
            Q0=makeQuery(id+"F29.imprint","IMPRINT",FACE,{"disambiguationData":[TD([[makeQuery(id+"F29.imprint","IMPRINT",EDGE,{"derivedFrom":sQuery(id+"F29.wireOp",EDGE,"E109.bottom")}),-1.0]])]});
            extrude(context, id + "F30", {"entities" : qUnion([Q0]), "operationType" : NewBodyOperationType.REMOVE, "endBound" : BoundingType.UP_TO_NEXT, "oppositeDirection" : true, "depth" : 30.48 * mm});
        }
        {
            var Q0;
            Q0=makeQuery(id+"F4.opExtrude","SWEPT_FACE",FACE,{"disambiguationData":[OSD([sQuery(id+"F3.wireOp",EDGE,"E25.10")])]});
            var sketch = newSketch(context, id + "F31", { "sketchPlane" : qUnion([Q0])});
            skLineSegment(sketch, "E112.bottom", {"start": v(-17830.8, 2771.78) * mm, "end": v(-17526, 2771.78) * mm});
            skLineSegment(sketch, "E112.top", {"start": v(-17830.8, 2466.98) * mm, "end": v(-17526, 2466.98) * mm});
            skLineSegment(sketch, "E112.left", {"start": v(-17830.8, 2771.78) * mm, "end": v(-17830.8, 2466.98) * mm});
            skLineSegment(sketch, "E112.right", {"start": v(-17526, 2771.78) * mm, "end": v(-17526, 2466.98) * mm});
            skSolve(sketch);
        }
        {
            var Q0;
            Q0=makeQuery(id+"F31.imprint","IMPRINT",FACE,{"disambiguationData":[TD([[makeQuery(id+"F31.imprint","IMPRINT",EDGE,{"derivedFrom":sQuery(id+"F31.wireOp",EDGE,"E112.bottom")}),1.0]])]});
            extrude(context, id + "F32", {"entities" : qUnion([Q0]), "operationType" : NewBodyOperationType.ADD, "endBound" : BoundingType.UP_TO_NEXT, "depth" : 30.48 * mm});
        }
        {
            var Q0;
            {var subQ0=sQuery(id+"F0.wireOp",EDGE,"E1");Q0=makeQuery(id+"F4.boolean.opBoolean","MERGE",FACE,{"derivedFrom":[makeQuery(id+"F1.opExtrude","SWEPT_FACE",FACE,{"disambiguationData":[OSD([subQ0])]}),makeQuery(id+"F4.opExtrude","SWEPT_FACE",FACE,{"disambiguationData":[OSD([subQ0])]})]});}
            var sketch = newSketch(context, id + "F33", { "sketchPlane" : qUnion([Q0])});
            skLineSegment(sketch, "E113.bottom", {"start": v(-12801.6, 2517.78) * mm, "end": v(-12039.6, 2517.78) * mm});
            skLineSegment(sketch, "E113.left", {"start": v(-12801.6, 2517.78) * mm, "end": v(-12801.6, 1755.78) * mm});
            skLineSegment(sketch, "E113.right", {"start": v(-12039.6, 2517.78) * mm, "end": v(-12039.6, 1755.78) * mm});
            skLineSegment(sketch, "E114.bottom", {"start": v(-10541, 2517.78) * mm, "end": v(-9779, 2517.78) * mm});
            skLineSegment(sketch, "E114.left", {"start": v(-10541, 2517.78) * mm, "end": v(-10541, 1755.78) * mm});
            skLineSegment(sketch, "E114.right", {"start": v(-9779, 2517.78) * mm, "end": v(-9779, 1755.78) * mm});
            skLineSegment(sketch, "E115.bottom", {"start": v(-8077.2, 2517.78) * mm, "end": v(-7315.2, 2517.78) * mm});
            skLineSegment(sketch, "E115.left", {"start": v(-8077.2, 2517.78) * mm, "end": v(-8077.2, 1755.78) * mm});
            skLineSegment(sketch, "E115.right", {"start": v(-7315.2, 2517.78) * mm, "end": v(-7315.2, 1755.78) * mm});
            skLineSegment(sketch, "E116.bottom", {"start": v(-5613.4, 2517.78) * mm, "end": v(-4851.4, 2517.78) * mm});
            skLineSegment(sketch, "E116.left", {"start": v(-5613.4, 2517.78) * mm, "end": v(-5613.4, 1755.78) * mm});
            skLineSegment(sketch, "E116.right", {"start": v(-4851.4, 2517.78) * mm, "end": v(-4851.4, 1755.78) * mm});
            skLineSegment(sketch, "E117", {"start": v(-12801.6, 1755.78) * mm, "end": v(-12420.6, 1755.78) * mm});
            skLineSegment(sketch, "E118", {"start": v(-12420.6, 1755.78) * mm, "end": v(-12039.6, 1755.78) * mm});
            skLineSegment(sketch, "E119", {"start": v(-10541, 1755.78) * mm, "end": v(-10160, 1755.78) * mm});
            skLineSegment(sketch, "E120", {"start": v(-10160, 1755.78) * mm, "end": v(-9779, 1755.78) * mm});
            skLineSegment(sketch, "E121", {"start": v(-8077.2, 1755.78) * mm, "end": v(-7696.2, 1755.78) * mm});
            skLineSegment(sketch, "E122", {"start": v(-7696.2, 1755.78) * mm, "end": v(-7315.2, 1755.78) * mm});
            skLineSegment(sketch, "E123", {"start": v(-5613.4, 1755.78) * mm, "end": v(-5232.4, 1755.78) * mm});
            skLineSegment(sketch, "E124", {"start": v(-5232.4, 1755.78) * mm, "end": v(-4851.4, 1755.78) * mm});
            skSolve(sketch);
        }
        {
            var Q0;
            Q0=makeQuery(id+"F33.imprint","IMPRINT",FACE,{"disambiguationData":[TD([[makeQuery(id+"F33.imprint","IMPRINT",EDGE,{"derivedFrom":sQuery(id+"F33.wireOp",EDGE,"E113.bottom")}),-1.0]])]});
            var Q1;
            Q1=makeQuery(id+"F33.imprint","IMPRINT",FACE,{"disambiguationData":[TD([[makeQuery(id+"F33.imprint","IMPRINT",EDGE,{"derivedFrom":sQuery(id+"F33.wireOp",EDGE,"E114.bottom")}),-1.0]])]});
            var Q2;
            Q2=makeQuery(id+"F33.imprint","IMPRINT",FACE,{"disambiguationData":[TD([[makeQuery(id+"F33.imprint","IMPRINT",EDGE,{"derivedFrom":sQuery(id+"F33.wireOp",EDGE,"E115.bottom")}),-1.0]])]});
            var Q3;
            Q3=makeQuery(id+"F33.imprint","IMPRINT",FACE,{"disambiguationData":[TD([[makeQuery(id+"F33.imprint","IMPRINT",EDGE,{"derivedFrom":sQuery(id+"F33.wireOp",EDGE,"E116.bottom")}),-1.0]])]});
            extrude(context, id + "F34", {"entities" : qUnion([Q0, Q1, Q2, Q3]), "operationType" : NewBodyOperationType.REMOVE, "endBound" : BoundingType.UP_TO_NEXT, "oppositeDirection" : true, "depth" : 30.48 * mm});
        }
        {
            var Q0;
            {var subQ2=sQuery(id+"F2.wireOp",EDGE,"E19");Q0=makeQuery(id+"F2.imprint","IMPRINT",FACE,{"disambiguationData":[TD([[makeQuery(id+"F2.imprint","IMPRINT",EDGE,{"derivedFrom":subQ2}),1.0]])]});}
            var sketch = newSketch(context, id + "F35", { "sketchPlane" : qUnion([Q0])});
            skLineSegment(sketch, "E125.bottom", {"start": v(1092.2, 11899.9) * mm, "end": v(1193.8, 11899.9) * mm});
            skLineSegment(sketch, "E125.top", {"start": v(1092.2, 8420.1) * mm, "end": v(1193.8, 8420.1) * mm});
            skLineSegment(sketch, "E125.left", {"start": v(1092.2, 11899.9) * mm, "end": v(1092.2, 8420.1) * mm});
            skLineSegment(sketch, "E125.right", {"start": v(1193.8, 11899.9) * mm, "end": v(1193.8, 8420.1) * mm});
            skLineSegment(sketch, "E126", {"start": v(1092.2, 8420.1) * mm, "end": v(152.4, 8420.1) * mm, "construction": true});
            skLineSegment(sketch, "E127", {"start": v(152.4, 8420.1) * mm, "end": v(152.4, 9779) * mm, "construction": true});
            skLineSegment(sketch, "E128", {"start": v(152.4, 11899.9) * mm, "end": v(152.4, 10541) * mm, "construction": true});
            skSolve(sketch);
        }
        {
            var Q0;
            Q0=makeQuery(id+"F35.imprint","IMPRINT",FACE,{"disambiguationData":[TD([[makeQuery(id+"F35.imprint","IMPRINT",EDGE,{"derivedFrom":sQuery(id+"F35.wireOp",EDGE,"E125.bottom")}),-1.0]])]});
            var Q1;
            {var subQ0=sQuery(id+"F3.wireOp",EDGE,"E25.18");var subQ1=sQuery(id+"F3.wireOp",EDGE,"E25.17");var subQ2=sQuery(id+"F3.wireOp",EDGE,"E25.16");var subQ3=sQuery(id+"F3.wireOp",EDGE,"E25.15");var subQ4=sQuery(id+"F3.wireOp",EDGE,"E25.14");var subQ5=sQuery(id+"F3.wireOp",EDGE,"E25.13");var subQ6=sQuery(id+"F3.wireOp",EDGE,"E25.12");var subQ7=sQuery(id+"F3.wireOp",EDGE,"E25.11");var subQ8=sQuery(id+"F3.wireOp",EDGE,"E25.10");var subQ9=sQuery(id+"F3.wireOp",EDGE,"E25.9");var subQ10=sQuery(id+"F3.wireOp",EDGE,"E25.8");var subQ11=sQuery(id+"F3.wireOp",EDGE,"E25.7");var subQ12=sQuery(id+"F3.wireOp",EDGE,"E25.6");var subQ13=sQuery(id+"F3.wireOp",EDGE,"E25.5");var subQ14=sQuery(id+"F3.wireOp",EDGE,"E25.4");var subQ15=sQuery(id+"F3.wireOp",EDGE,"E25.3");var subQ16=sQuery(id+"F3.wireOp",EDGE,"E25.2");var subQ17=sQuery(id+"F3.wireOp",EDGE,"E25.1");var subQ18=sQuery(id+"F3.wireOp",EDGE,"E25.0");var subQ19=sQuery(id+"F2.wireOp",EDGE,"E23");var subQ20=sQuery(id+"F2.wireOp",EDGE,"E21");var subQ21=sQuery(id+"F2.wireOp",EDGE,"E20");var subQ22=sQuery(id+"F2.wireOp",EDGE,"E19");var subQ23=sQuery(id+"F0.wireOp",EDGE,"E15");var subQ24=sQuery(id+"F0.wireOp",EDGE,"E14");var subQ25=sQuery(id+"F0.wireOp",EDGE,"E13");var subQ26=sQuery(id+"F0.wireOp",EDGE,"E12");var subQ27=sQuery(id+"F0.wireOp",EDGE,"E11");var subQ28=sQuery(id+"F0.wireOp",EDGE,"E10");var subQ29=sQuery(id+"F0.wireOp",EDGE,"E9");var subQ30=sQuery(id+"F0.wireOp",EDGE,"E8");var subQ31=sQuery(id+"F0.wireOp",EDGE,"E6");var subQ32=sQuery(id+"F0.wireOp",EDGE,"E5");var subQ33=sQuery(id+"F0.wireOp",EDGE,"E4");var subQ34=sQuery(id+"F0.wireOp",EDGE,"E3");var subQ35=sQuery(id+"F0.wireOp",EDGE,"E2");var subQ36=sQuery(id+"F0.wireOp",EDGE,"E1");var subQ37=sQuery(id+"F0.wireOp",EDGE,"E0");Q1=makeQuery(id+"F32.boolean.opBoolean","MERGE",FACE,{"derivedFrom":[makeQuery(id+"F6.boolean.opBoolean","MERGE",FACE,{"derivedFrom":[makeQuery(id+"F4.opExtrude","CAP_FACE",FACE,{"disambiguationData":[OSD([subQ37,subQ36,subQ35,subQ34,subQ33,subQ32,subQ31,subQ30,subQ29,subQ28,subQ27,subQ26,subQ25,subQ24,subQ23,subQ22,subQ21,subQ20,subQ19,subQ18,subQ17,subQ16,subQ15,subQ14,subQ13,subQ12,subQ11,subQ10,subQ9,subQ8,subQ7,subQ6,subQ5,subQ4,subQ3,subQ2,subQ1,subQ0])],"isStart":false}),makeQuery(id+"F6.opExtrude","CAP_FACE",FACE,{"disambiguationData":[OSD([subQ37,subQ36,subQ35,subQ34,subQ33,subQ32,subQ31,subQ30,subQ29,subQ28,subQ27,subQ26,subQ25,subQ24,subQ23,subQ22,subQ21,subQ20,subQ19,subQ18,subQ17,subQ16,subQ15,subQ14,subQ13,subQ12,subQ11,subQ10,subQ9,subQ8,subQ7,subQ6,subQ5,subQ4,subQ3,subQ2,subQ1,subQ0])],"isStart":false})]}),makeQuery(id+"F32.opExtrude","SWEPT_FACE",FACE,{"disambiguationData":[OSD([sQuery(id+"F31.wireOp",EDGE,"E112.bottom")])]})]});}
            extrude(context, id + "F36", {"entities" : qUnion([Q0]), "operationType" : NewBodyOperationType.ADD, "endBound" : BoundingType.UP_TO_SURFACE, "endBoundEntityFace" : qUnion([Q1]), "depth" : 30.48 * mm});
        }
        {
            var Q0;
            Q0=makeQuery(id+"F36.opExtrude","SWEPT_FACE",FACE,{"disambiguationData":[OSD([sQuery(id+"F35.wireOp",EDGE,"E125.right")])]});
            var sketch = newSketch(context, id + "F37", { "sketchPlane" : qUnion([Q0])});
            skLineSegment(sketch, "E129.bottom", {"start": v(8420.1, 2771.78) * mm, "end": v(9334.5, 2771.78) * mm});
            skLineSegment(sketch, "E129.top", {"start": v(8420.1, 1247.78) * mm, "end": v(9334.5, 1247.78) * mm});
            skLineSegment(sketch, "E129.left", {"start": v(8420.1, 2771.78) * mm, "end": v(8420.1, 1247.78) * mm});
            skLineSegment(sketch, "E129.right", {"start": v(9334.5, 2771.78) * mm, "end": v(9334.5, 1247.78) * mm});
            skSolve(sketch);
        }
        {
            var Q0;
            Q0=makeQuery(id+"F37.imprint","IMPRINT",FACE,{"disambiguationData":[TD([[makeQuery(id+"F37.imprint","IMPRINT",EDGE,{"derivedFrom":sQuery(id+"F37.wireOp",EDGE,"E129.bottom")}),1.0]])]});
            extrude(context, id + "F38", {"entities" : qUnion([Q0]), "operationType" : NewBodyOperationType.REMOVE, "endBound" : BoundingType.UP_TO_NEXT, "oppositeDirection" : true, "depth" : 30.48 * mm});
        }
        {
            var Q0;
            {var subQ2=sQuery(id+"F2.wireOp",EDGE,"E19");Q0=makeQuery(id+"F2.imprint","IMPRINT",FACE,{"disambiguationData":[TD([[makeQuery(id+"F2.imprint","IMPRINT",EDGE,{"derivedFrom":subQ2}),1.0]])]});}
            var sketch = newSketch(context, id + "F39", { "sketchPlane" : qUnion([Q0])});
            skLineSegment(sketch, "E130.bottom", {"start": v(1092.2, 11899.9) * mm, "end": v(152.4, 11899.9) * mm});
            skLineSegment(sketch, "E130.top", {"start": v(1092.2, 8420.1) * mm, "end": v(152.4, 8420.1) * mm});
            skLineSegment(sketch, "E130.left", {"start": v(1092.2, 11899.9) * mm, "end": v(1092.2, 8420.1) * mm});
            skLineSegment(sketch, "E130.right", {"start": v(152.4, 11899.9) * mm, "end": v(152.4, 8420.1) * mm});
            skSolve(sketch);
        }
        {
            var Q0;
            Q0 = qSketchRegion(id + "F39", true);
            extrude(context, id + "F40", {"entities" : qUnion([Q0]), "operationType" : NewBodyOperationType.REMOVE, "endBound" : BoundingType.UP_TO_NEXT, "oppositeDirection" : true, "depth" : 30.48 * mm});
        }
        {
            var Q0;
            {var subQ1=sQuery(id+"F3.wireOp",EDGE,"E25.17");var subQ2=sQuery(id+"F3.wireOp",EDGE,"E25.16");Q0=makeQuery(id+"F40.boolean.opBoolean","MERGE",FACE,{"derivedFrom":[makeQuery(id+"F6.boolean.opBoolean","SPLIT",FACE,{"disambiguationData":[TD([makeQuery(id+"F4.opExtrude","SWEPT_FACE",FACE,{"disambiguationData":[OSD([subQ2])]})])],"derivedFrom":makeQuery(id+"F4.opExtrude","SWEPT_FACE",FACE,{"disambiguationData":[OSD([subQ1])]})}),makeQuery(id+"F40.opExtrude","SWEPT_FACE",FACE,{"disambiguationData":[OSD([sQuery(id+"F39.wireOp",EDGE,"E130.right")])]})]});}
            var sketch = newSketch(context, id + "F41", { "sketchPlane" : qUnion([Q0])});
            skLineSegment(sketch, "E131", {"start": v(8420.1, -254) * mm, "end": v(8420.1, 0) * mm});
            skLineSegment(sketch, "E132", {"start": v(9789.26, -254) * mm, "end": v(9611.46, -254) * mm, "construction": true});
            skLineSegment(sketch, "E133", {"start": v(9611.46, -254) * mm, "end": v(9611.46, -127) * mm});
            skLineSegment(sketch, "E134", {"start": v(9611.46, -127) * mm, "end": v(9433.66, -127) * mm});
            skLineSegment(sketch, "E135", {"start": v(9433.66, -127) * mm, "end": v(9433.66, 0) * mm});
            skLineSegment(sketch, "E136", {"start": v(9433.66, 0) * mm, "end": v(8420.1, 0) * mm});
            skLineSegment(sketch, "E137", {"start": v(8420.1, -254) * mm, "end": v(9611.46, -254) * mm});
            skLineSegment(sketch, "E138", {"start": v(8420.1, 0) * mm, "end": v(8420.1, -254) * mm});
            skSolve(sketch);
        }
        {
            var Q0;
            Q0=makeQuery(id+"F41.imprint","IMPRINT",FACE,{"disambiguationData":[TD([[makeQuery(id+"F41.imprint","IMPRINT",EDGE,{"derivedFrom":sQuery(id+"F41.wireOp",EDGE,"E133")}),1.0]])]});
            extrude(context, id + "F42", {"entities" : qUnion([Q0]), "operationType" : NewBodyOperationType.ADD, "endBound" : BoundingType.UP_TO_NEXT, "depth" : 30.48 * mm});
        }
    });
